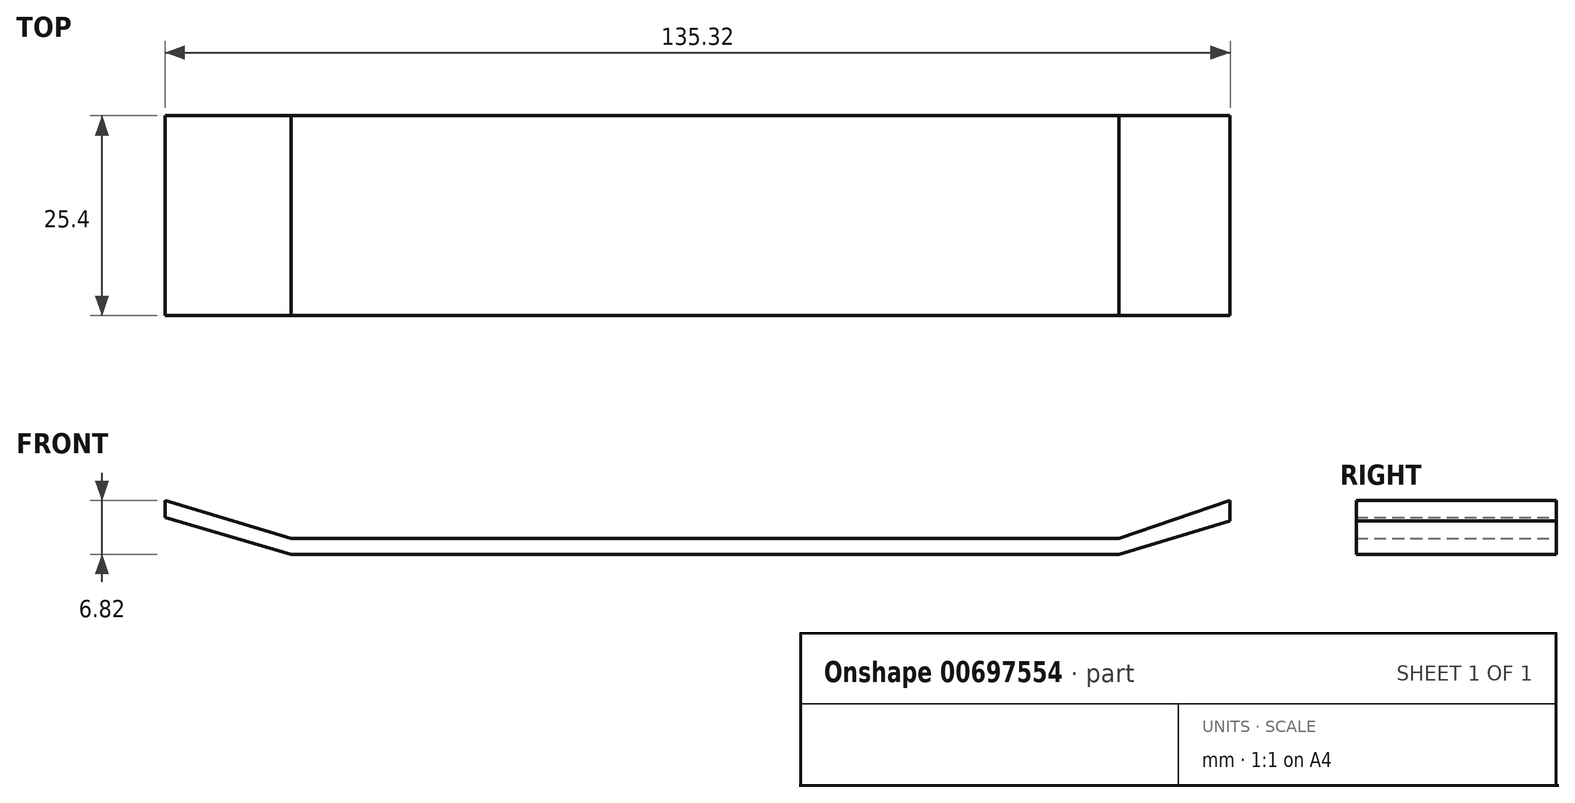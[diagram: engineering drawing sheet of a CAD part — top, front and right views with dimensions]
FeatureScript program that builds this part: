
annotation { "Feature Type Name" : "Feature", "Feature Type Description" : "" }
export const myFeature = defineFeature(function(context is Context, id is Id, definition is map)
    precondition{}
    {
        {
            var Q0;
            Q0=qCreatedBy(makeId("Front.planeOp"),FACE);
            var sketch = newSketch(context, id + "F0", { "sketchPlane" : qUnion([Q0])});
            skLineSegment(sketch, "E0.bottom", {"start": v(-51.65, 0) * mm, "end": v(53.54, 0) * mm});
            skLineSegment(sketch, "E0.top", {"start": v(-51.65, -2) * mm, "end": v(53.54, -2) * mm});
            skLineSegment(sketch, "E0.left", {"start": v(-51.65, 0) * mm, "end": v(-51.65, -2) * mm});
            skLineSegment(sketch, "E0.right", {"start": v(53.54, 0) * mm, "end": v(53.54, -2) * mm});
            skLineSegment(sketch, "E1", {"start": v(-51.65, 0) * mm, "end": v(-67.66, 4.82) * mm});
            skLineSegment(sketch, "E2", {"start": v(-67.66, 2.7) * mm, "end": v(-51.65, -2) * mm});
            skLineSegment(sketch, "E3", {"start": v(53.54, 0) * mm, "end": v(67.66, 4.82) * mm});
            skLineSegment(sketch, "E4", {"start": v(67.66, 4.82) * mm, "end": v(67.66, 2.24) * mm});
            skLineSegment(sketch, "E5", {"start": v(67.66, 2.24) * mm, "end": v(53.54, -2) * mm});
            skLineSegment(sketch, "E6", {"start": v(-67.66, 2.7) * mm, "end": v(-67.66, 4.82) * mm});
            skSolve(sketch);
        }
        {
            var Q0;
            Q0 = qSketchRegion(id + "F0", true);
            extrude(context, id + "F1", {"entities" : qUnion([Q0]), "depth" : 25.4 * mm, "offsetDistance" : 25.4 * mm});
        }
    });
